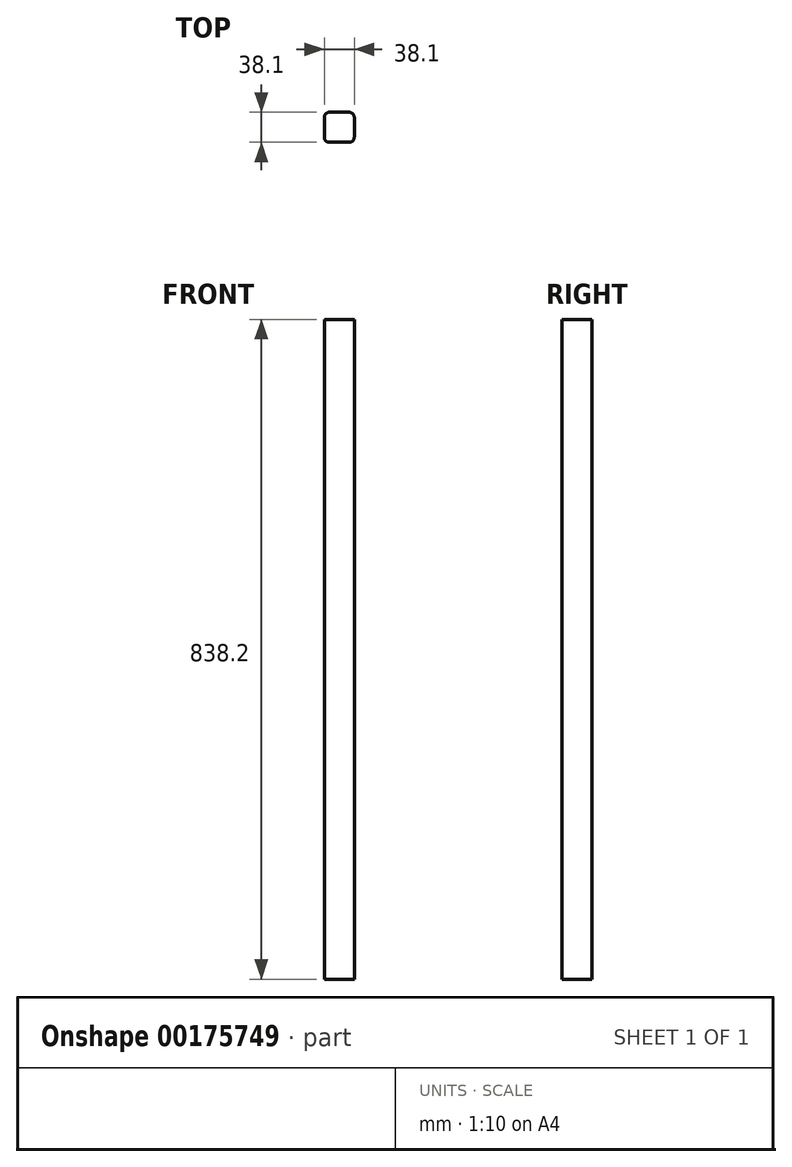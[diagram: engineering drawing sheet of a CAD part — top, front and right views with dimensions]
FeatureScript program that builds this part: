
annotation { "Feature Type Name" : "Feature", "Feature Type Description" : "" }
export const myFeature = defineFeature(function(context is Context, id is Id, definition is map)
    precondition{}
    {
        {
            var Q0;
            Q0=qCreatedBy(makeId("Top.planeOp"),FACE);
            var sketch = newSketch(context, id + "F0", { "sketchPlane" : qUnion([Q0])});
            skLineSegment(sketch, "E0.bottom", {"start": v(12.7, 19.05) * mm, "end": v(-12.7, 19.05) * mm});
            skLineSegment(sketch, "E0.top", {"start": v(12.7, -19.05) * mm, "end": v(-12.7, -19.05) * mm});
            skLineSegment(sketch, "E0.left", {"start": v(19.05, 12.7) * mm, "end": v(19.05, -12.7) * mm});
            skLineSegment(sketch, "E0.right", {"start": v(-19.05, 12.7) * mm, "end": v(-19.05, -12.7) * mm});
            skPoint(sketch, "E0.middle", {"position": v(0, 0) * mm});
            skPoint(sketch, "E1.visualSharp", {"position": v(19.05, 19.05) * mm});
            skArc(sketch, "E1.filletArc", {"start": v(19.05, 12.7) * mm, "mid": v(17.2, 17.2) * mm, "end": v(12.7, 19.05) * mm});
            skPoint(sketch, "E2.visualSharp", {"position": v(-19.05, 19.05) * mm});
            skArc(sketch, "E2.filletArc", {"start": v(-12.7, 19.05) * mm, "mid": v(-17.2, 17.2) * mm, "end": v(-19.05, 12.7) * mm});
            skPoint(sketch, "E3.visualSharp", {"position": v(-19.05, -19.05) * mm});
            skArc(sketch, "E3.filletArc", {"start": v(-19.05, -12.7) * mm, "mid": v(-17.2, -17.2) * mm, "end": v(-12.7, -19.05) * mm});
            skPoint(sketch, "E4.visualSharp", {"position": v(19.05, -19.05) * mm});
            skArc(sketch, "E4.filletArc", {"start": v(12.7, -19.05) * mm, "mid": v(17.2, -17.2) * mm, "end": v(19.05, -12.7) * mm});
            skSolve(sketch);
        }
        {
            var Q0;
            Q0 = qSketchRegion(id + "F0", true);
            extrude(context, id + "F1", {"entities" : qUnion([Q0]), "depth" : 838.2 * mm});
        }
    });
